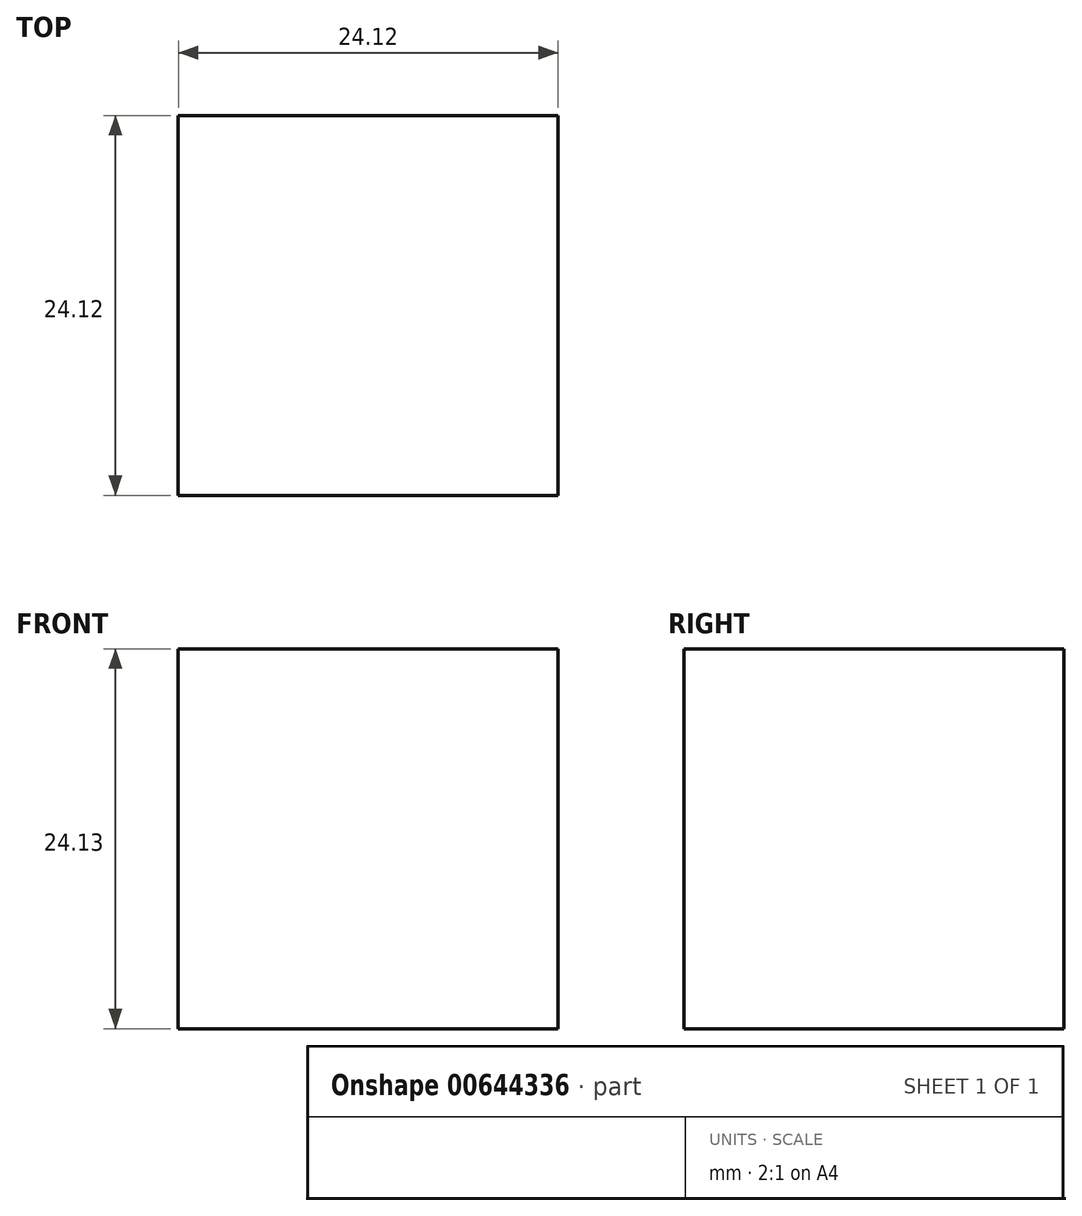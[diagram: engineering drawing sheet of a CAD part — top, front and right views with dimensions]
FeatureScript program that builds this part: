
annotation { "Feature Type Name" : "Feature", "Feature Type Description" : "" }
export const myFeature = defineFeature(function(context is Context, id is Id, definition is map)
    precondition{}
    {
        {
            var Q0;
            Q0=qCreatedBy(makeId("Top.planeOp"),FACE);
            var sketch = newSketch(context, id + "F0", { "sketchPlane" : qUnion([Q0])});
            skLineSegment(sketch, "E0.bottom", {"start": v(12.07, 12.07) * mm, "end": v(-12.07, 12.07) * mm});
            skLineSegment(sketch, "E0.top", {"start": v(12.07, -12.06) * mm, "end": v(-12.07, -12.06) * mm});
            skLineSegment(sketch, "E0.left", {"start": v(12.07, 12.06) * mm, "end": v(12.07, -12.06) * mm});
            skLineSegment(sketch, "E0.right", {"start": v(-12.07, 12.06) * mm, "end": v(-12.07, -12.06) * mm});
            skPoint(sketch, "E0.middle", {"position": v(0, 0) * mm});
            skSolve(sketch);
        }
        {
            var Q0;
            Q0 = qSketchRegion(id + "F0", true);
            extrude(context, id + "F1", {"entities" : qUnion([Q0]), "depth" : 24.13 * mm, "offsetDistance" : 25.4 * mm});
        }
    });
